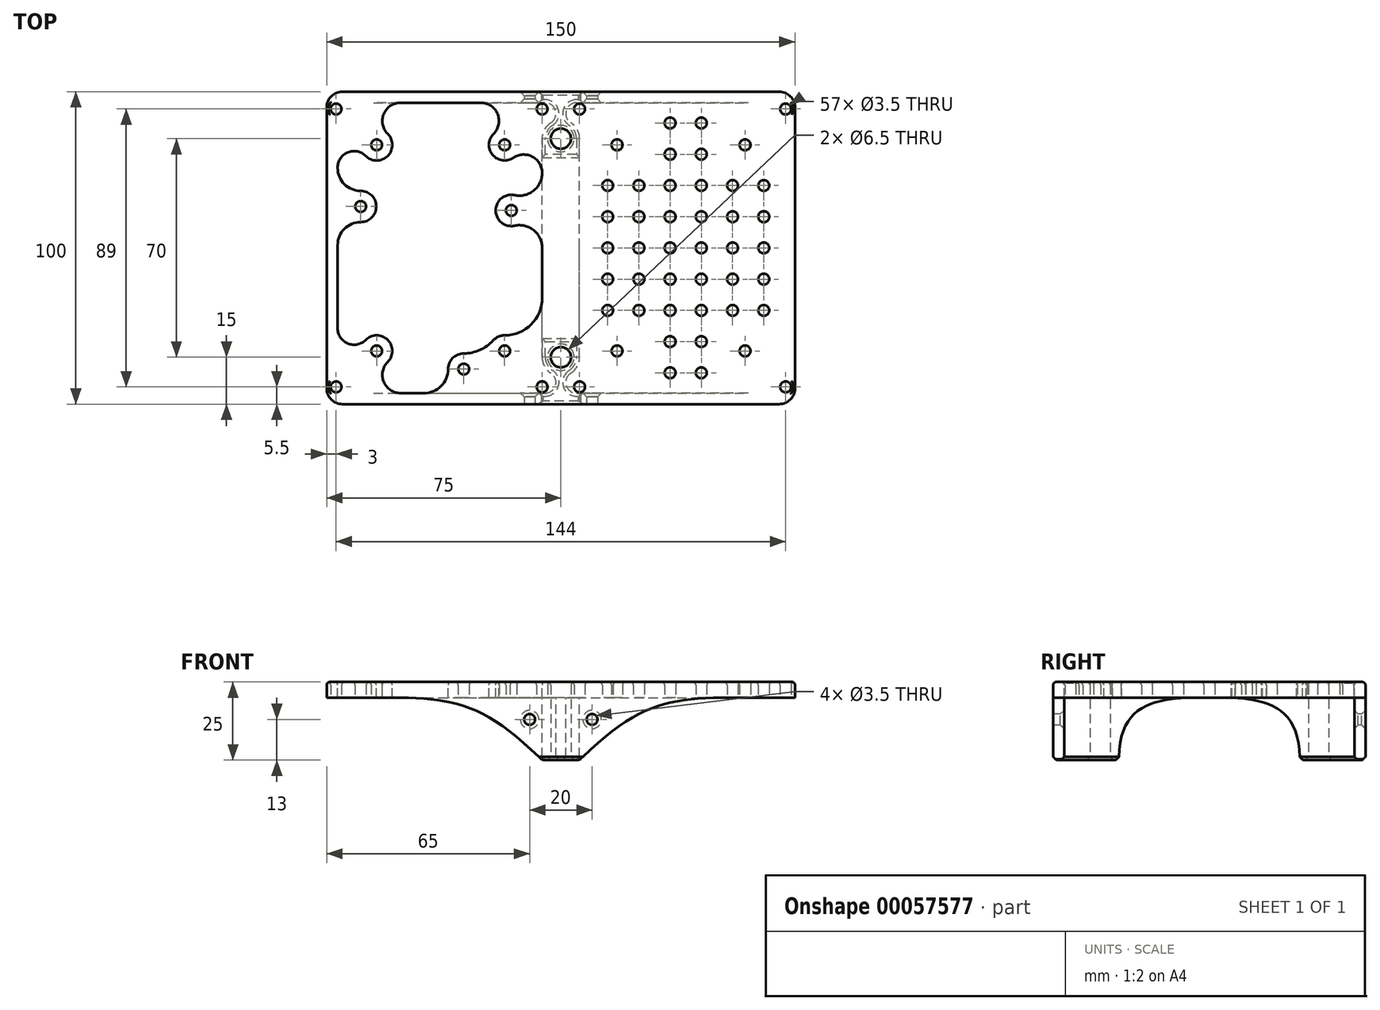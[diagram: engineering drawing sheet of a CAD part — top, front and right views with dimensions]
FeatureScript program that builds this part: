
annotation { "Feature Type Name" : "Feature", "Feature Type Description" : "" }
export const myFeature = defineFeature(function(context is Context, id is Id, definition is map)
    precondition{}
    {
        {
            var Q0;
            Q0=qCreatedBy(makeId("Top.planeOp"),FACE);
            var sketch = newSketch(context, id + "F0", { "sketchPlane" : qUnion([Q0])});
            skCircle(sketch, "E0", {"center": v(0, 35) * mm, "radius": 3.25 * mm});
            skCircle(sketch, "E1", {"center": v(0, -35) * mm, "radius": 3.25 * mm});
            skLineSegment(sketch, "E2", {"start": v(0, 35) * mm, "end": v(0, 0) * mm, "construction": true});
            skLineSegment(sketch, "E3", {"start": v(0, 0) * mm, "end": v(0, -35) * mm, "construction": true});
            skLineSegment(sketch, "E4.bottom", {"start": v(-75, 41.25) * mm, "end": v(-5, 41.25) * mm, "construction": true});
            skLineSegment(sketch, "E4.top", {"start": v(-75, -41.25) * mm, "end": v(-5, -41.25) * mm, "construction": true});
            skLineSegment(sketch, "E4.left", {"start": v(-75, 41.25) * mm, "end": v(-75, -41.25) * mm, "construction": true});
            skLineSegment(sketch, "E4.right", {"start": v(-5, 41.25) * mm, "end": v(-5, -41.25) * mm, "construction": true});
            skPoint(sketch, "E5", {"position": v(-64.13, -36.25) * mm});
            skLineSegment(sketch, "E6", {"start": v(-75, -36.25) * mm, "end": v(-5, -36.25) * mm, "construction": true});
            skCircle(sketch, "E7", {"center": v(-31.1, -38.8) * mm, "radius": 1.75 * mm});
            skCircle(sketch, "E8", {"center": v(-64.13, 13.28) * mm, "radius": 1.75 * mm});
            skCircle(sketch, "E9", {"center": v(-15.87, 12) * mm, "radius": 1.75 * mm});
            skPoint(sketch, "E10", {"position": v(-15.87, -36.25) * mm});
            skLineSegment(sketch, "E11", {"start": v(-75, 16.69) * mm, "end": v(-5, 16.7) * mm, "construction": true});
            skCircle(sketch, "E12", {"center": v(0, 0) * mm, "radius": 75 * mm, "construction": true});
            skLineSegment(sketch, "E13.rect.bottom", {"start": v(75, 50) * mm, "end": v(-75, 50) * mm});
            skLineSegment(sketch, "E13.rect.top", {"start": v(75, -50) * mm, "end": v(-75, -50) * mm});
            skLineSegment(sketch, "E13.rect.left", {"start": v(75, 50) * mm, "end": v(75, -50) * mm});
            skLineSegment(sketch, "E13.rect.right", {"start": v(-75, 50) * mm, "end": v(-75, -50) * mm});
            skCircle(sketch, "E14", {"center": v(0, -35) * mm, "radius": 6 * mm, "construction": true});
            skCircle(sketch, "E15", {"center": v(0, 35) * mm, "radius": 6 * mm, "construction": true});
            skLineSegment(sketch, "E16.bottom", {"start": v(-62, 36) * mm, "end": v(-15, 36) * mm, "construction": true});
            skLineSegment(sketch, "E16.top", {"start": v(-62, -36) * mm, "end": v(-15, -36) * mm, "construction": true});
            skLineSegment(sketch, "E16.left", {"start": v(-62, 36) * mm, "end": v(-62, -36) * mm, "construction": true});
            skLineSegment(sketch, "E16.right", {"start": v(-15, 36) * mm, "end": v(-15, -36) * mm, "construction": true});
            skLineSegment(sketch, "E17.0", {"start": v(-59, 33) * mm, "end": v(-18, 33) * mm, "construction": true});
            skLineSegment(sketch, "E17.1", {"start": v(-59, 33) * mm, "end": v(-59, -33) * mm, "construction": true});
            skLineSegment(sketch, "E17.2", {"start": v(-59, -33) * mm, "end": v(-18, -33) * mm, "construction": true});
            skLineSegment(sketch, "E17.3", {"start": v(-18, 33) * mm, "end": v(-18, -33) * mm, "construction": true});
            skCircle(sketch, "E18", {"center": v(-59, 33) * mm, "radius": 1.75 * mm});
            skCircle(sketch, "E19", {"center": v(-18, 33) * mm, "radius": 1.75 * mm});
            skCircle(sketch, "E20", {"center": v(-59, -33) * mm, "radius": 1.75 * mm});
            skCircle(sketch, "E21", {"center": v(-18, -33) * mm, "radius": 1.75 * mm});
            skLineSegment(sketch, "E22.bottom", {"start": v(-75, 47.5) * mm, "end": v(-3, 47.5) * mm, "construction": true});
            skLineSegment(sketch, "E22.top", {"start": v(-75, -47.5) * mm, "end": v(-3, -47.5) * mm, "construction": true});
            skLineSegment(sketch, "E22.left", {"start": v(-75, 47.5) * mm, "end": v(-75, -47.5) * mm, "construction": true});
            skLineSegment(sketch, "E22.right", {"start": v(-3, 47.5) * mm, "end": v(-3, -47.5) * mm, "construction": true});
            skLineSegment(sketch, "E23.0", {"start": v(-72, 44.5) * mm, "end": v(-72, -44.5) * mm, "construction": true});
            skLineSegment(sketch, "E23.1", {"start": v(-72, 44.5) * mm, "end": v(-6, 44.5) * mm, "construction": true});
            skLineSegment(sketch, "E23.2", {"start": v(-6, 44.5) * mm, "end": v(-6, -44.5) * mm, "construction": true});
            skLineSegment(sketch, "E23.3", {"start": v(-72, -44.5) * mm, "end": v(-6, -44.5) * mm, "construction": true});
            skCircle(sketch, "E24", {"center": v(-72, 44.5) * mm, "radius": 1.75 * mm});
            skCircle(sketch, "E25", {"center": v(-6, 44.5) * mm, "radius": 1.75 * mm});
            skCircle(sketch, "E26", {"center": v(-72, -44.5) * mm, "radius": 1.75 * mm});
            skCircle(sketch, "E27", {"center": v(-6, -44.5) * mm, "radius": 1.75 * mm});
            skCircle(sketch, "E28.MirrorC", {"center": v(72, 44.5) * mm, "radius": 1.75 * mm});
            skCircle(sketch, "E29.MirrorC", {"center": v(6, 44.5) * mm, "radius": 1.75 * mm});
            skCircle(sketch, "E30.MirrorC", {"center": v(59, 33) * mm, "radius": 1.75 * mm});
            skCircle(sketch, "E31.MirrorC", {"center": v(18, 33) * mm, "radius": 1.75 * mm});
            skCircle(sketch, "E32.MirrorC", {"center": v(59, -33) * mm, "radius": 1.75 * mm});
            skCircle(sketch, "E33.MirrorC", {"center": v(18, -33) * mm, "radius": 1.75 * mm});
            skCircle(sketch, "E34.MirrorC", {"center": v(6, -44.5) * mm, "radius": 1.75 * mm});
            skCircle(sketch, "E35.MirrorC", {"center": v(72, -44.5) * mm, "radius": 1.75 * mm});
            skCircle(sketch, "E36", {"center": v(65, 40) * mm, "radius": 1.75 * mm, "construction": true});
            skCircle(sketch, "E37.0.1.0", {"center": v(65, 30) * mm, "radius": 1.75 * mm, "construction": true});
            skCircle(sketch, "E37.0.2.0", {"center": v(65, 20) * mm, "radius": 1.75 * mm});
            skCircle(sketch, "E37.0.3.0", {"center": v(65, 10) * mm, "radius": 1.75 * mm});
            skCircle(sketch, "E37.0.4.0", {"center": v(65, 0) * mm, "radius": 1.75 * mm});
            skCircle(sketch, "E37.0.5.0", {"center": v(65, -10) * mm, "radius": 1.75 * mm});
            skCircle(sketch, "E37.0.6.0", {"center": v(65, -20) * mm, "radius": 1.75 * mm});
            skCircle(sketch, "E37.0.7.0", {"center": v(65, -30) * mm, "radius": 1.75 * mm, "construction": true});
            skCircle(sketch, "E37.0.8.0", {"center": v(65, -40) * mm, "radius": 1.75 * mm, "construction": true});
            skCircle(sketch, "E37.1.0.0", {"center": v(55, 40) * mm, "radius": 1.75 * mm, "construction": true});
            skCircle(sketch, "E37.1.1.0", {"center": v(55, 30) * mm, "radius": 1.75 * mm, "construction": true});
            skCircle(sketch, "E37.1.2.0", {"center": v(55, 20) * mm, "radius": 1.75 * mm});
            skCircle(sketch, "E37.1.3.0", {"center": v(55, 10) * mm, "radius": 1.75 * mm});
            skCircle(sketch, "E37.1.4.0", {"center": v(55, 0) * mm, "radius": 1.75 * mm});
            skCircle(sketch, "E37.1.5.0", {"center": v(55, -10) * mm, "radius": 1.75 * mm});
            skCircle(sketch, "E37.1.6.0", {"center": v(55, -20) * mm, "radius": 1.75 * mm});
            skCircle(sketch, "E37.1.7.0", {"center": v(55, -30) * mm, "radius": 1.75 * mm, "construction": true});
            skCircle(sketch, "E37.1.8.0", {"center": v(55, -40) * mm, "radius": 1.75 * mm, "construction": true});
            skCircle(sketch, "E37.2.0.0", {"center": v(45, 40) * mm, "radius": 1.75 * mm});
            skCircle(sketch, "E37.2.1.0", {"center": v(45, 30) * mm, "radius": 1.75 * mm});
            skCircle(sketch, "E37.2.2.0", {"center": v(45, 20) * mm, "radius": 1.75 * mm});
            skCircle(sketch, "E37.2.3.0", {"center": v(45, 10) * mm, "radius": 1.75 * mm});
            skCircle(sketch, "E37.2.4.0", {"center": v(45, 0) * mm, "radius": 1.75 * mm});
            skCircle(sketch, "E37.2.5.0", {"center": v(45, -10) * mm, "radius": 1.75 * mm});
            skCircle(sketch, "E37.2.6.0", {"center": v(45, -20) * mm, "radius": 1.75 * mm});
            skCircle(sketch, "E37.2.7.0", {"center": v(45, -30) * mm, "radius": 1.75 * mm});
            skCircle(sketch, "E37.2.8.0", {"center": v(45, -40) * mm, "radius": 1.75 * mm});
            skCircle(sketch, "E37.3.0.0", {"center": v(35, 40) * mm, "radius": 1.75 * mm});
            skCircle(sketch, "E37.3.1.0", {"center": v(35, 30) * mm, "radius": 1.75 * mm});
            skCircle(sketch, "E37.3.2.0", {"center": v(35, 20) * mm, "radius": 1.75 * mm});
            skCircle(sketch, "E37.3.3.0", {"center": v(35, 10) * mm, "radius": 1.75 * mm});
            skCircle(sketch, "E37.3.4.0", {"center": v(35, 0) * mm, "radius": 1.75 * mm});
            skCircle(sketch, "E37.3.5.0", {"center": v(35, -10) * mm, "radius": 1.75 * mm});
            skCircle(sketch, "E37.3.6.0", {"center": v(35, -20) * mm, "radius": 1.75 * mm});
            skCircle(sketch, "E37.3.7.0", {"center": v(35, -30) * mm, "radius": 1.75 * mm});
            skCircle(sketch, "E37.3.8.0", {"center": v(35, -40) * mm, "radius": 1.75 * mm});
            skCircle(sketch, "E37.4.0.0", {"center": v(25, 40) * mm, "radius": 1.75 * mm, "construction": true});
            skCircle(sketch, "E37.4.1.0", {"center": v(25, 30) * mm, "radius": 1.75 * mm, "construction": true});
            skCircle(sketch, "E37.4.2.0", {"center": v(25, 20) * mm, "radius": 1.75 * mm});
            skCircle(sketch, "E37.4.3.0", {"center": v(25, 10) * mm, "radius": 1.75 * mm});
            skCircle(sketch, "E37.4.4.0", {"center": v(25, 0) * mm, "radius": 1.75 * mm});
            skCircle(sketch, "E37.4.5.0", {"center": v(25, -10) * mm, "radius": 1.75 * mm});
            skCircle(sketch, "E37.4.6.0", {"center": v(25, -20) * mm, "radius": 1.75 * mm});
            skCircle(sketch, "E37.4.7.0", {"center": v(25, -30) * mm, "radius": 1.75 * mm, "construction": true});
            skCircle(sketch, "E37.4.8.0", {"center": v(25, -40) * mm, "radius": 1.75 * mm, "construction": true});
            skCircle(sketch, "E37.5.0.0", {"center": v(15, 40) * mm, "radius": 1.75 * mm, "construction": true});
            skCircle(sketch, "E37.5.1.0", {"center": v(15, 30) * mm, "radius": 1.75 * mm, "construction": true});
            skCircle(sketch, "E37.5.2.0", {"center": v(15, 20) * mm, "radius": 1.75 * mm});
            skCircle(sketch, "E37.5.3.0", {"center": v(15, 10) * mm, "radius": 1.75 * mm});
            skCircle(sketch, "E37.5.4.0", {"center": v(15, 0) * mm, "radius": 1.75 * mm});
            skCircle(sketch, "E37.5.5.0", {"center": v(15, -10) * mm, "radius": 1.75 * mm});
            skCircle(sketch, "E37.5.6.0", {"center": v(15, -20) * mm, "radius": 1.75 * mm});
            skCircle(sketch, "E37.5.7.0", {"center": v(15, -30) * mm, "radius": 1.75 * mm, "construction": true});
            skCircle(sketch, "E37.5.8.0", {"center": v(15, -40) * mm, "radius": 1.75 * mm, "construction": true});
            skCircle(sketch, "E37.6.0.0", {"center": v(5, 40) * mm, "radius": 1.75 * mm, "construction": true});
            skCircle(sketch, "E37.6.1.0", {"center": v(5, 30) * mm, "radius": 1.75 * mm, "construction": true});
            skCircle(sketch, "E37.6.2.0", {"center": v(5, 20) * mm, "radius": 1.75 * mm, "construction": true});
            skCircle(sketch, "E37.6.3.0", {"center": v(5, 10) * mm, "radius": 1.75 * mm, "construction": true});
            skCircle(sketch, "E37.6.4.0", {"center": v(5, 0) * mm, "radius": 1.75 * mm, "construction": true});
            skCircle(sketch, "E37.6.5.0", {"center": v(5, -10) * mm, "radius": 1.75 * mm, "construction": true});
            skCircle(sketch, "E37.6.6.0", {"center": v(5, -20) * mm, "radius": 1.75 * mm, "construction": true});
            skCircle(sketch, "E37.6.7.0", {"center": v(5, -30) * mm, "radius": 1.75 * mm, "construction": true});
            skCircle(sketch, "E37.6.8.0", {"center": v(5, -40) * mm, "radius": 1.75 * mm, "construction": true});
            skLineSegment(sketch, "E37.direction1", {"start": v(65, 40) * mm, "end": v(55, 40) * mm, "construction": true});
            skLineSegment(sketch, "E37.direction2", {"start": v(65, 40) * mm, "end": v(65, 30) * mm, "construction": true});
            skSolve(sketch);
        }
        {
            var Q0;
            Q0 = qSketchRegion(id + "F0", true);
            extrude(context, id + "F1", {"entities" : qUnion([Q0]), "depth" : 5 * mm});
        }
        {
            var Q0;
            Q0=makeQuery(id+"F1.opExtrude","SWEPT_EDGE",EDGE,{"disambiguationData":[OSD([sQuery(id+"F0.wireOp",EDGE,"E13.rect.bottom"),sQuery(id+"F0.wireOp",EDGE,"E13.rect.right")])]});
            var Q1;
            Q1=makeQuery(id+"F1.opExtrude","SWEPT_EDGE",EDGE,{"disambiguationData":[OSD([sQuery(id+"F0.wireOp",EDGE,"E13.rect.top"),sQuery(id+"F0.wireOp",EDGE,"E13.rect.right")])]});
            var Q2;
            Q2=makeQuery(id+"F1.opExtrude","SWEPT_EDGE",EDGE,{"disambiguationData":[OSD([sQuery(id+"F0.wireOp",EDGE,"E13.rect.bottom"),sQuery(id+"F0.wireOp",EDGE,"E13.rect.left")])]});
            var Q3;
            Q3=makeQuery(id+"F1.opExtrude","SWEPT_EDGE",EDGE,{"disambiguationData":[OSD([sQuery(id+"F0.wireOp",EDGE,"E13.rect.top"),sQuery(id+"F0.wireOp",EDGE,"E13.rect.left")])]});
            fillet(context, id + "F2", {"entities" : qUnion([Q0, Q1, Q2, Q3]), "radius" : 5 * mm, "tangentPropagation" : true, "allowEdgeOverflow" : false});
        }
        {
            var Q0;
            Q0=makeQuery(id+"F1.opExtrude","CAP_FACE",FACE,{"disambiguationData":[OSD([sQuery(id+"F0.wireOp",EDGE,"E0"),sQuery(id+"F0.wireOp",EDGE,"E1"),sQuery(id+"F0.wireOp",EDGE,"E7"),sQuery(id+"F0.wireOp",EDGE,"E8"),sQuery(id+"F0.wireOp",EDGE,"E9"),sQuery(id+"F0.wireOp",EDGE,"E13.rect.bottom"),sQuery(id+"F0.wireOp",EDGE,"E13.rect.top"),sQuery(id+"F0.wireOp",EDGE,"E13.rect.left"),sQuery(id+"F0.wireOp",EDGE,"E13.rect.right"),sQuery(id+"F0.wireOp",EDGE,"E18"),sQuery(id+"F0.wireOp",EDGE,"E19"),sQuery(id+"F0.wireOp",EDGE,"E20"),sQuery(id+"F0.wireOp",EDGE,"E21"),sQuery(id+"F0.wireOp",EDGE,"E24"),sQuery(id+"F0.wireOp",EDGE,"E25"),sQuery(id+"F0.wireOp",EDGE,"E26"),sQuery(id+"F0.wireOp",EDGE,"E27"),sQuery(id+"F0.wireOp",EDGE,"E28.MirrorC"),sQuery(id+"F0.wireOp",EDGE,"E29.MirrorC"),sQuery(id+"F0.wireOp",EDGE,"E30.MirrorC"),sQuery(id+"F0.wireOp",EDGE,"E31.MirrorC"),sQuery(id+"F0.wireOp",EDGE,"E32.MirrorC"),sQuery(id+"F0.wireOp",EDGE,"E33.MirrorC"),sQuery(id+"F0.wireOp",EDGE,"E34.MirrorC"),sQuery(id+"F0.wireOp",EDGE,"E35.MirrorC"),sQuery(id+"F0.wireOp",EDGE,"E37.0.2.0"),sQuery(id+"F0.wireOp",EDGE,"E37.0.3.0"),sQuery(id+"F0.wireOp",EDGE,"E37.0.4.0"),sQuery(id+"F0.wireOp",EDGE,"E37.0.5.0"),sQuery(id+"F0.wireOp",EDGE,"E37.0.6.0"),sQuery(id+"F0.wireOp",EDGE,"E37.1.2.0"),sQuery(id+"F0.wireOp",EDGE,"E37.1.3.0"),sQuery(id+"F0.wireOp",EDGE,"E37.1.4.0"),sQuery(id+"F0.wireOp",EDGE,"E37.1.5.0"),sQuery(id+"F0.wireOp",EDGE,"E37.1.6.0"),sQuery(id+"F0.wireOp",EDGE,"E37.2.0.0"),sQuery(id+"F0.wireOp",EDGE,"E37.2.1.0"),sQuery(id+"F0.wireOp",EDGE,"E37.2.2.0"),sQuery(id+"F0.wireOp",EDGE,"E37.2.3.0"),sQuery(id+"F0.wireOp",EDGE,"E37.2.4.0"),sQuery(id+"F0.wireOp",EDGE,"E37.2.5.0"),sQuery(id+"F0.wireOp",EDGE,"E37.2.6.0"),sQuery(id+"F0.wireOp",EDGE,"E37.2.7.0"),sQuery(id+"F0.wireOp",EDGE,"E37.2.8.0"),sQuery(id+"F0.wireOp",EDGE,"E37.3.0.0"),sQuery(id+"F0.wireOp",EDGE,"E37.3.1.0"),sQuery(id+"F0.wireOp",EDGE,"E37.3.2.0"),sQuery(id+"F0.wireOp",EDGE,"E37.3.3.0"),sQuery(id+"F0.wireOp",EDGE,"E37.3.4.0"),sQuery(id+"F0.wireOp",EDGE,"E37.3.5.0"),sQuery(id+"F0.wireOp",EDGE,"E37.3.6.0"),sQuery(id+"F0.wireOp",EDGE,"E37.3.7.0"),sQuery(id+"F0.wireOp",EDGE,"E37.3.8.0"),sQuery(id+"F0.wireOp",EDGE,"E37.4.2.0"),sQuery(id+"F0.wireOp",EDGE,"E37.4.3.0"),sQuery(id+"F0.wireOp",EDGE,"E37.4.4.0"),sQuery(id+"F0.wireOp",EDGE,"E37.4.5.0"),sQuery(id+"F0.wireOp",EDGE,"E37.4.6.0"),sQuery(id+"F0.wireOp",EDGE,"E37.5.2.0"),sQuery(id+"F0.wireOp",EDGE,"E37.5.3.0"),sQuery(id+"F0.wireOp",EDGE,"E37.5.4.0"),sQuery(id+"F0.wireOp",EDGE,"E37.5.5.0"),sQuery(id+"F0.wireOp",EDGE,"E37.5.6.0")])],"isStart":false});
            var sketch = newSketch(context, id + "F3", { "sketchPlane" : qUnion([Q0])});
            skCircle(sketch, "E38", {"center": v(-59, 33) * mm, "radius": 5 * mm, "construction": true});
            skCircle(sketch, "E39", {"center": v(-64.13, 13.28) * mm, "radius": 5 * mm, "construction": true});
            skCircle(sketch, "E40", {"center": v(-18, 33) * mm, "radius": 5 * mm, "construction": true});
            skCircle(sketch, "E41", {"center": v(-15.87, 12) * mm, "radius": 5 * mm, "construction": true});
            skCircle(sketch, "E42", {"center": v(-18, -33) * mm, "radius": 5 * mm, "construction": true});
            skCircle(sketch, "E43", {"center": v(-31.1, -38.8) * mm, "radius": 5 * mm, "construction": true});
            skCircle(sketch, "E44", {"center": v(-59, -33) * mm, "radius": 5 * mm, "construction": true});
            skLineSegment(sketch, "E45.0", {"start": v(70, -46.5) * mm, "end": v(-71.5, -46.5) * mm, "construction": true});
            skLineSegment(sketch, "E45.1", {"start": v(-71.5, 46.5) * mm, "end": v(-71.5, -46.5) * mm, "construction": true});
            skLineSegment(sketch, "E45.2", {"start": v(70, 46.5) * mm, "end": v(-71.5, 46.5) * mm, "construction": true});
            skArc(sketch, "E46", {"start": v(-64.13, 8.28) * mm, "mid": v(-69.34, 6.12) * mm, "end": v(-71.5, 0.9) * mm});
            skArc(sketch, "E47", {"start": v(-71.5, -25.75) * mm, "mid": v(-68.26, -30.6) * mm, "end": v(-62.54, -29.46) * mm});
            skArc(sketch, "E48", {"start": v(-31.1, -33.8) * mm, "mid": v(-25.96, -32.7) * mm, "end": v(-21.7, -29.63) * mm});
            skLineSegment(sketch, "E49", {"start": v(-6, 46.5) * mm, "end": v(-6, -46.5) * mm, "construction": true});
            skArc(sketch, "E50", {"start": v(-18, -28) * mm, "mid": v(-9.51, -24.49) * mm, "end": v(-6, -16) * mm});
            skArc(sketch, "E51", {"start": v(-6, 0) * mm, "mid": v(-8.7, 5.67) * mm, "end": v(-14.82, 7.12) * mm});
            skArc(sketch, "E52", {"start": v(-14.82, 16.9) * mm, "mid": v(-8.7, 18.35) * mm, "end": v(-6, 24.02) * mm});
            skArc(sketch, "E53", {"start": v(-21.54, 36.54) * mm, "mid": v(-20.27, 42.9) * mm, "end": v(-25.66, 46.5) * mm});
            skArc(sketch, "E54", {"start": v(-6, 24.02) * mm, "mid": v(-9.13, 29.21) * mm, "end": v(-15.18, 28.87) * mm});
            skArc(sketch, "E55", {"start": v(-71.5, 25.65) * mm, "mid": v(-69.34, 20.44) * mm, "end": v(-64.13, 18.28) * mm});
            skArc(sketch, "E56", {"start": v(-62.54, 29.46) * mm, "mid": v(-68.26, 30.6) * mm, "end": v(-71.5, 25.75) * mm});
            skArc(sketch, "E57", {"start": v(-51.34, 46.5) * mm, "mid": v(-56.73, 42.9) * mm, "end": v(-55.46, 36.54) * mm});
            skArc(sketch, "E58", {"start": v(-55.46, -36.54) * mm, "mid": v(-56.73, -42.9) * mm, "end": v(-51.34, -46.5) * mm});
            skArc(sketch, "E59", {"start": v(-43.82, -46.5) * mm, "mid": v(-38.37, -44.24) * mm, "end": v(-36.1, -38.8) * mm});
            skLineSegment(sketch, "E60", {"start": v(-66.25, -25.75) * mm, "end": v(-59, -33) * mm, "construction": true});
            skLineSegment(sketch, "E61", {"start": v(-59, -33) * mm, "end": v(-51.34, -40.66) * mm, "construction": true});
            skArc(sketch, "E62", {"start": v(-55.46, -36.54) * mm, "mid": v(-55.46, -29.46) * mm, "end": v(-62.54, -29.46) * mm});
            skLineSegment(sketch, "E63", {"start": v(-71.5, 25.65) * mm, "end": v(-71.5, 25.75) * mm});
            skLineSegment(sketch, "E64", {"start": v(-64.13, 18.28) * mm, "end": v(-64.13, 18.28) * mm});
            skArc(sketch, "E65", {"start": v(-64.13, 8.28) * mm, "mid": v(-59.13, 13.28) * mm, "end": v(-64.13, 18.28) * mm});
            skLineSegment(sketch, "E66", {"start": v(-71.5, 0.9) * mm, "end": v(-71.5, -25.75) * mm});
            skLineSegment(sketch, "E67", {"start": v(-51.34, -46.5) * mm, "end": v(-43.82, -46.5) * mm, "construction": true});
            skLineSegment(sketch, "E68", {"start": v(-51.34, 46.5) * mm, "end": v(-25.66, 46.5) * mm});
            skArc(sketch, "E69", {"start": v(-55.46, 36.54) * mm, "mid": v(-55.46, 29.46) * mm, "end": v(-62.54, 29.46) * mm});
            skArc(sketch, "E70", {"start": v(-15.18, 28.87) * mm, "mid": v(-21.85, 29.8) * mm, "end": v(-21.54, 36.54) * mm});
            skArc(sketch, "E71", {"start": v(-14.82, 7.12) * mm, "mid": v(-20.87, 12) * mm, "end": v(-14.82, 16.9) * mm});
            skArc(sketch, "E72", {"start": v(-36.1, -38.8) * mm, "mid": v(-34.65, -35.25) * mm, "end": v(-31.1, -33.8) * mm});
            skArc(sketch, "E73", {"start": v(-21.7, -29.63) * mm, "mid": v(-20.02, -28.43) * mm, "end": v(-18, -28) * mm});
            skLineSegment(sketch, "E74", {"start": v(-6, -16) * mm, "end": v(-6, 0) * mm});
            skLineSegment(sketch, "E75", {"start": v(-51.34, -46.5) * mm, "end": v(-43.82, -46.5) * mm});
            skSolve(sketch);
        }
        {
            var Q0;
            Q0 = qSketchRegion(id + "F3", true);
            extrude(context, id + "F4", {"entities" : qUnion([Q0]), "operationType" : NewBodyOperationType.REMOVE, "endBound" : BoundingType.THROUGH_ALL, "oppositeDirection" : true, "depth" : 25 * mm});
        }
        {
            var Q0;
            Q0=makeQuery(id+"F1.opExtrude","CAP_FACE",FACE,{"disambiguationData":[OSD([sQuery(id+"F0.wireOp",EDGE,"E0"),sQuery(id+"F0.wireOp",EDGE,"E1"),sQuery(id+"F0.wireOp",EDGE,"E7"),sQuery(id+"F0.wireOp",EDGE,"E8"),sQuery(id+"F0.wireOp",EDGE,"E9"),sQuery(id+"F0.wireOp",EDGE,"E13.rect.bottom"),sQuery(id+"F0.wireOp",EDGE,"E13.rect.top"),sQuery(id+"F0.wireOp",EDGE,"E13.rect.left"),sQuery(id+"F0.wireOp",EDGE,"E13.rect.right"),sQuery(id+"F0.wireOp",EDGE,"E18"),sQuery(id+"F0.wireOp",EDGE,"E19"),sQuery(id+"F0.wireOp",EDGE,"E20"),sQuery(id+"F0.wireOp",EDGE,"E21"),sQuery(id+"F0.wireOp",EDGE,"E24"),sQuery(id+"F0.wireOp",EDGE,"E25"),sQuery(id+"F0.wireOp",EDGE,"E26"),sQuery(id+"F0.wireOp",EDGE,"E27"),sQuery(id+"F0.wireOp",EDGE,"E28.MirrorC"),sQuery(id+"F0.wireOp",EDGE,"E29.MirrorC"),sQuery(id+"F0.wireOp",EDGE,"E30.MirrorC"),sQuery(id+"F0.wireOp",EDGE,"E31.MirrorC"),sQuery(id+"F0.wireOp",EDGE,"E32.MirrorC"),sQuery(id+"F0.wireOp",EDGE,"E33.MirrorC"),sQuery(id+"F0.wireOp",EDGE,"E34.MirrorC"),sQuery(id+"F0.wireOp",EDGE,"E35.MirrorC"),sQuery(id+"F0.wireOp",EDGE,"E37.0.2.0"),sQuery(id+"F0.wireOp",EDGE,"E37.0.3.0"),sQuery(id+"F0.wireOp",EDGE,"E37.0.4.0"),sQuery(id+"F0.wireOp",EDGE,"E37.0.5.0"),sQuery(id+"F0.wireOp",EDGE,"E37.0.6.0"),sQuery(id+"F0.wireOp",EDGE,"E37.1.2.0"),sQuery(id+"F0.wireOp",EDGE,"E37.1.3.0"),sQuery(id+"F0.wireOp",EDGE,"E37.1.4.0"),sQuery(id+"F0.wireOp",EDGE,"E37.1.5.0"),sQuery(id+"F0.wireOp",EDGE,"E37.1.6.0"),sQuery(id+"F0.wireOp",EDGE,"E37.2.0.0"),sQuery(id+"F0.wireOp",EDGE,"E37.2.1.0"),sQuery(id+"F0.wireOp",EDGE,"E37.2.2.0"),sQuery(id+"F0.wireOp",EDGE,"E37.2.3.0"),sQuery(id+"F0.wireOp",EDGE,"E37.2.4.0"),sQuery(id+"F0.wireOp",EDGE,"E37.2.5.0"),sQuery(id+"F0.wireOp",EDGE,"E37.2.6.0"),sQuery(id+"F0.wireOp",EDGE,"E37.2.7.0"),sQuery(id+"F0.wireOp",EDGE,"E37.2.8.0"),sQuery(id+"F0.wireOp",EDGE,"E37.3.0.0"),sQuery(id+"F0.wireOp",EDGE,"E37.3.1.0"),sQuery(id+"F0.wireOp",EDGE,"E37.3.2.0"),sQuery(id+"F0.wireOp",EDGE,"E37.3.3.0"),sQuery(id+"F0.wireOp",EDGE,"E37.3.4.0"),sQuery(id+"F0.wireOp",EDGE,"E37.3.5.0"),sQuery(id+"F0.wireOp",EDGE,"E37.3.6.0"),sQuery(id+"F0.wireOp",EDGE,"E37.3.7.0"),sQuery(id+"F0.wireOp",EDGE,"E37.3.8.0"),sQuery(id+"F0.wireOp",EDGE,"E37.4.2.0"),sQuery(id+"F0.wireOp",EDGE,"E37.4.3.0"),sQuery(id+"F0.wireOp",EDGE,"E37.4.4.0"),sQuery(id+"F0.wireOp",EDGE,"E37.4.5.0"),sQuery(id+"F0.wireOp",EDGE,"E37.4.6.0"),sQuery(id+"F0.wireOp",EDGE,"E37.5.2.0"),sQuery(id+"F0.wireOp",EDGE,"E37.5.3.0"),sQuery(id+"F0.wireOp",EDGE,"E37.5.4.0"),sQuery(id+"F0.wireOp",EDGE,"E37.5.5.0"),sQuery(id+"F0.wireOp",EDGE,"E37.5.6.0")])],"isStart":true});
            var sketch = newSketch(context, id + "F5", { "sketchPlane" : qUnion([Q0])});
            skArc(sketch, "E76", {"start": v(-6, 35) * mm, "mid": v(0, 41) * mm, "end": v(6, 35) * mm, "construction": true});
            skArc(sketch, "E77", {"start": v(6, -35) * mm, "mid": v(0, -41) * mm, "end": v(-6, -35) * mm, "construction": true});
            skLineSegment(sketch, "E78", {"start": v(-6, 35) * mm, "end": v(-6, -35) * mm});
            skLineSegment(sketch, "E79", {"start": v(6, 35) * mm, "end": v(6, -35) * mm});
            skLineSegment(sketch, "E80.bottom", {"start": v(-60, 50) * mm, "end": v(60, 50) * mm});
            skLineSegment(sketch, "E80.top", {"start": v(-60, 46.5) * mm, "end": v(60, 46.5) * mm, "construction": true});
            skLineSegment(sketch, "E80.left", {"start": v(-60, 50) * mm, "end": v(-60, 46.5) * mm});
            skLineSegment(sketch, "E80.right", {"start": v(60, 50) * mm, "end": v(60, 46.5) * mm});
            skLineSegment(sketch, "E81.bottom", {"start": v(-60, -50) * mm, "end": v(60, -50) * mm});
            skLineSegment(sketch, "E81.top", {"start": v(-60, -46.5) * mm, "end": v(60, -46.5) * mm, "construction": true});
            skLineSegment(sketch, "E81.left", {"start": v(-60, -50) * mm, "end": v(-60, -46.5) * mm});
            skLineSegment(sketch, "E81.right", {"start": v(60, -50) * mm, "end": v(60, -46.5) * mm});
            skPoint(sketch, "E82", {"position": v(0, 46.5) * mm});
            skPoint(sketch, "E83", {"position": v(0, -46.5) * mm});
            skArc(sketch, "E84", {"start": v(-3.2, 40.07) * mm, "mid": v(-1.72, 43.99) * mm, "end": v(-5.06, 46.5) * mm});
            skPoint(sketch, "E85", {"position": v(-6, 44.5) * mm});
            skLineSegment(sketch, "E86", {"start": v(-6, 44.5) * mm, "end": v(-5.06, 43.02) * mm, "construction": true});
            skLineSegment(sketch, "E87", {"start": v(-3.2, 40.07) * mm, "end": v(-5.06, 43.02) * mm, "construction": true});
            skArc(sketch, "E88.MirrorCS", {"start": v(3.2, 40.07) * mm, "mid": v(1.72, 43.99) * mm, "end": v(5.06, 46.5) * mm});
            skArc(sketch, "E89.MirrorCS", {"start": v(-3.2, -40.07) * mm, "mid": v(-1.72, -43.99) * mm, "end": v(-5.06, -46.5) * mm});
            skArc(sketch, "E90.MirrorCS", {"start": v(3.2, -40.07) * mm, "mid": v(1.72, -43.99) * mm, "end": v(5.06, -46.5) * mm});
            skLineSegment(sketch, "E91", {"start": v(-5.06, -46.5) * mm, "end": v(-60, -46.5) * mm});
            skLineSegment(sketch, "E92", {"start": v(5.06, -46.5) * mm, "end": v(60, -46.5) * mm});
            skLineSegment(sketch, "E93", {"start": v(-60, 46.5) * mm, "end": v(-5.06, 46.5) * mm});
            skLineSegment(sketch, "E94", {"start": v(5.06, 46.5) * mm, "end": v(60, 46.5) * mm});
            skArc(sketch, "E95", {"start": v(-6, 35) * mm, "mid": v(-5.25, 37.9) * mm, "end": v(-3.2, 40.07) * mm});
            skArc(sketch, "E96", {"start": v(3.2, 40.07) * mm, "mid": v(5.25, 37.9) * mm, "end": v(6, 35) * mm});
            skArc(sketch, "E97", {"start": v(6, -35) * mm, "mid": v(5.25, -37.9) * mm, "end": v(3.2, -40.07) * mm});
            skArc(sketch, "E98", {"start": v(-3.2, -40.07) * mm, "mid": v(-5.25, -37.9) * mm, "end": v(-6, -35) * mm});
            skCircle(sketch, "E99.0", {"center": v(0, -35) * mm, "radius": 3.25 * mm});
            skCircle(sketch, "E99.1", {"center": v(0, 35) * mm, "radius": 3.25 * mm});
            skSolve(sketch);
        }
        {
            var Q0;
            Q0 = qSketchRegion(id + "F5", true);
            extrude(context, id + "F6", {"entities" : qUnion([Q0]), "operationType" : NewBodyOperationType.ADD, "depth" : 20 * mm});
        }
        {
            var Q0;
            Q0=qCreatedBy(makeId("Front.planeOp"),FACE);
            var sketch = newSketch(context, id + "F7", { "sketchPlane" : qUnion([Q0])});
            skLineSegment(sketch, "E100", {"start": v(-60, 0) * mm, "end": v(-60, -20) * mm});
            skLineSegment(sketch, "E101", {"start": v(-60, -20) * mm, "end": v(-6, -20) * mm});
            skFitSpline(sketch, "E102", {"points": [v(-60, 0) * mm, v(-6, -20) * mm], "startDerivative": vector(71.9, 0) * mm, "endDerivative": vector(61.29, -60) * mm});
            skFitSpline(sketch, "E103.MirrorCS", {"points": [v(60, 0) * mm, v(6, -20) * mm], "startDerivative": vector(-71.9, 0) * mm, "endDerivative": vector(-61.29, -60) * mm});
            skLineSegment(sketch, "E104.MirrorCS", {"start": v(60, 0) * mm, "end": v(60, -20) * mm});
            skLineSegment(sketch, "E105.MirrorCS", {"start": v(60, -20) * mm, "end": v(6, -20) * mm});
            skSolve(sketch);
        }
        {
            var Q0;
            Q0 = qSketchRegion(id + "F7", true);
            extrude(context, id + "F8", {"entities" : qUnion([Q0]), "operationType" : NewBodyOperationType.REMOVE, "endBound" : BoundingType.THROUGH_ALL, "oppositeDirection" : true, "depth" : 25 * mm, "hasSecondDirection" : true, "secondDirectionBound" : SecondDirectionBoundingType.THROUGH_ALL, "secondDirectionOppositeDirection" : false, "secondDirectionDepth" : 25 * mm});
        }
        {
            var Q0;
            Q0=makeQuery(id+"F6.opExtrude","SWEPT_FACE",FACE,{"disambiguationData":[OSD([sQuery(id+"F5.wireOp",EDGE,"E79")])]});
            var sketch = newSketch(context, id + "F9", { "sketchPlane" : qUnion([Q0])});
            skFitSpline(sketch, "E106", {"points": [v(-29, -20) * mm, v(0, 0) * mm, v(29, -20) * mm], "startDerivative": vector(0, 120) * mm, "endDerivative": vector(0, -120) * mm});
            skLineSegment(sketch, "E107", {"start": v(-29, -20) * mm, "end": v(29, -20) * mm});
            skSolve(sketch);
        }
        {
            var Q0;
            Q0 = qSketchRegion(id + "F9", true);
            extrude(context, id + "F10", {"entities" : qUnion([Q0]), "operationType" : NewBodyOperationType.REMOVE, "endBound" : BoundingType.THROUGH_ALL, "oppositeDirection" : true, "depth" : 25 * mm});
        }
        {
            var Q0;
            Q0=makeQuery(id+"F1.opExtrude","CAP_FACE",FACE,{"disambiguationData":[OSD([sQuery(id+"F0.wireOp",EDGE,"E0"),sQuery(id+"F0.wireOp",EDGE,"E1"),sQuery(id+"F0.wireOp",EDGE,"E7"),sQuery(id+"F0.wireOp",EDGE,"E8"),sQuery(id+"F0.wireOp",EDGE,"E9"),sQuery(id+"F0.wireOp",EDGE,"E13.rect.bottom"),sQuery(id+"F0.wireOp",EDGE,"E13.rect.top"),sQuery(id+"F0.wireOp",EDGE,"E13.rect.left"),sQuery(id+"F0.wireOp",EDGE,"E13.rect.right"),sQuery(id+"F0.wireOp",EDGE,"E18"),sQuery(id+"F0.wireOp",EDGE,"E19"),sQuery(id+"F0.wireOp",EDGE,"E20"),sQuery(id+"F0.wireOp",EDGE,"E21"),sQuery(id+"F0.wireOp",EDGE,"E24"),sQuery(id+"F0.wireOp",EDGE,"E25"),sQuery(id+"F0.wireOp",EDGE,"E26"),sQuery(id+"F0.wireOp",EDGE,"E27"),sQuery(id+"F0.wireOp",EDGE,"E28.MirrorC"),sQuery(id+"F0.wireOp",EDGE,"E29.MirrorC"),sQuery(id+"F0.wireOp",EDGE,"E30.MirrorC"),sQuery(id+"F0.wireOp",EDGE,"E31.MirrorC"),sQuery(id+"F0.wireOp",EDGE,"E32.MirrorC"),sQuery(id+"F0.wireOp",EDGE,"E33.MirrorC"),sQuery(id+"F0.wireOp",EDGE,"E34.MirrorC"),sQuery(id+"F0.wireOp",EDGE,"E35.MirrorC"),sQuery(id+"F0.wireOp",EDGE,"E37.0.2.0"),sQuery(id+"F0.wireOp",EDGE,"E37.0.3.0"),sQuery(id+"F0.wireOp",EDGE,"E37.0.4.0"),sQuery(id+"F0.wireOp",EDGE,"E37.0.5.0"),sQuery(id+"F0.wireOp",EDGE,"E37.0.6.0"),sQuery(id+"F0.wireOp",EDGE,"E37.1.2.0"),sQuery(id+"F0.wireOp",EDGE,"E37.1.3.0"),sQuery(id+"F0.wireOp",EDGE,"E37.1.4.0"),sQuery(id+"F0.wireOp",EDGE,"E37.1.5.0"),sQuery(id+"F0.wireOp",EDGE,"E37.1.6.0"),sQuery(id+"F0.wireOp",EDGE,"E37.2.0.0"),sQuery(id+"F0.wireOp",EDGE,"E37.2.1.0"),sQuery(id+"F0.wireOp",EDGE,"E37.2.2.0"),sQuery(id+"F0.wireOp",EDGE,"E37.2.3.0"),sQuery(id+"F0.wireOp",EDGE,"E37.2.4.0"),sQuery(id+"F0.wireOp",EDGE,"E37.2.5.0"),sQuery(id+"F0.wireOp",EDGE,"E37.2.6.0"),sQuery(id+"F0.wireOp",EDGE,"E37.2.7.0"),sQuery(id+"F0.wireOp",EDGE,"E37.2.8.0"),sQuery(id+"F0.wireOp",EDGE,"E37.3.0.0"),sQuery(id+"F0.wireOp",EDGE,"E37.3.1.0"),sQuery(id+"F0.wireOp",EDGE,"E37.3.2.0"),sQuery(id+"F0.wireOp",EDGE,"E37.3.3.0"),sQuery(id+"F0.wireOp",EDGE,"E37.3.4.0"),sQuery(id+"F0.wireOp",EDGE,"E37.3.5.0"),sQuery(id+"F0.wireOp",EDGE,"E37.3.6.0"),sQuery(id+"F0.wireOp",EDGE,"E37.3.7.0"),sQuery(id+"F0.wireOp",EDGE,"E37.3.8.0"),sQuery(id+"F0.wireOp",EDGE,"E37.4.2.0"),sQuery(id+"F0.wireOp",EDGE,"E37.4.3.0"),sQuery(id+"F0.wireOp",EDGE,"E37.4.4.0"),sQuery(id+"F0.wireOp",EDGE,"E37.4.5.0"),sQuery(id+"F0.wireOp",EDGE,"E37.4.6.0"),sQuery(id+"F0.wireOp",EDGE,"E37.5.2.0"),sQuery(id+"F0.wireOp",EDGE,"E37.5.3.0"),sQuery(id+"F0.wireOp",EDGE,"E37.5.4.0"),sQuery(id+"F0.wireOp",EDGE,"E37.5.5.0"),sQuery(id+"F0.wireOp",EDGE,"E37.5.6.0")])],"isStart":false});
            fillet(context, id + "F11", {"entities" : qUnion([Q0]), "radius" : 1 * mm, "tangentPropagation" : true, "allowEdgeOverflow" : false});
        }
        {
            var Q0;
            {var subQ0=sQuery(id+"F5.wireOp",EDGE,"E84");var subQ1=sQuery(id+"F5.wireOp",EDGE,"E80.bottom");var subQ2=sQuery(id+"F5.wireOp",EDGE,"E79");var subQ3=sQuery(id+"F5.wireOp",EDGE,"E88.MirrorCS");var subQ4=sQuery(id+"F5.wireOp",EDGE,"E78");var subQ5=sQuery(id+"F5.wireOp",EDGE,"E93");var subQ6=sQuery(id+"F5.wireOp",EDGE,"E94");var subQ7=sQuery(id+"F5.wireOp",EDGE,"E95");var subQ8=sQuery(id+"F5.wireOp",EDGE,"E96");var subQ9=sQuery(id+"F5.wireOp",EDGE,"E99.1");Q0=makeQuery(id+"F10.boolean.opBoolean","SPLIT",FACE,{"disambiguationData":[TD([makeQuery(id+"F1.opExtrude","SWEPT_FACE",FACE,{"disambiguationData":[OSD([sQuery(id+"F0.wireOp",EDGE,"E1")])]})])],"derivedFrom":makeQuery(id+"F6.opExtrude","CAP_FACE",FACE,{"disambiguationData":[OSD([subQ4,subQ2,subQ1,sQuery(id+"F5.wireOp",EDGE,"E80.left"),sQuery(id+"F5.wireOp",EDGE,"E80.right"),sQuery(id+"F5.wireOp",EDGE,"E81.bottom"),sQuery(id+"F5.wireOp",EDGE,"E81.left"),sQuery(id+"F5.wireOp",EDGE,"E81.right"),subQ0,subQ3,sQuery(id+"F5.wireOp",EDGE,"E89.MirrorCS"),sQuery(id+"F5.wireOp",EDGE,"E90.MirrorCS"),sQuery(id+"F5.wireOp",EDGE,"E91"),sQuery(id+"F5.wireOp",EDGE,"E92"),subQ5,subQ6,subQ7,subQ8,sQuery(id+"F5.wireOp",EDGE,"E97"),sQuery(id+"F5.wireOp",EDGE,"E98"),sQuery(id+"F5.wireOp",EDGE,"E99.0"),subQ9])],"isStart":false})});}
            var Q1;
            {var subQ0=sQuery(id+"F5.wireOp",EDGE,"E91");var subQ1=sQuery(id+"F5.wireOp",EDGE,"E78");var subQ2=sQuery(id+"F5.wireOp",EDGE,"E90.MirrorCS");var subQ3=sQuery(id+"F5.wireOp",EDGE,"E89.MirrorCS");var subQ4=sQuery(id+"F5.wireOp",EDGE,"E81.bottom");var subQ5=sQuery(id+"F5.wireOp",EDGE,"E79");var subQ6=sQuery(id+"F5.wireOp",EDGE,"E97");var subQ7=sQuery(id+"F5.wireOp",EDGE,"E92");var subQ8=sQuery(id+"F5.wireOp",EDGE,"E98");var subQ9=sQuery(id+"F5.wireOp",EDGE,"E99.0");Q1=makeQuery(id+"F10.boolean.opBoolean","SPLIT",FACE,{"disambiguationData":[TD([makeQuery(id+"F1.opExtrude","SWEPT_FACE",FACE,{"disambiguationData":[OSD([sQuery(id+"F0.wireOp",EDGE,"E0")])]})])],"derivedFrom":makeQuery(id+"F6.opExtrude","CAP_FACE",FACE,{"disambiguationData":[OSD([subQ1,subQ5,sQuery(id+"F5.wireOp",EDGE,"E80.bottom"),sQuery(id+"F5.wireOp",EDGE,"E80.left"),sQuery(id+"F5.wireOp",EDGE,"E80.right"),subQ4,sQuery(id+"F5.wireOp",EDGE,"E81.left"),sQuery(id+"F5.wireOp",EDGE,"E81.right"),sQuery(id+"F5.wireOp",EDGE,"E84"),sQuery(id+"F5.wireOp",EDGE,"E88.MirrorCS"),subQ3,subQ2,subQ0,subQ7,sQuery(id+"F5.wireOp",EDGE,"E93"),sQuery(id+"F5.wireOp",EDGE,"E94"),sQuery(id+"F5.wireOp",EDGE,"E95"),sQuery(id+"F5.wireOp",EDGE,"E96"),subQ6,subQ8,subQ9,sQuery(id+"F5.wireOp",EDGE,"E99.1")])],"isStart":false})});}
            var Q2;
            Q2=makeQuery(id+"F1.opExtrude","CAP_FACE",FACE,{"disambiguationData":[OSD([sQuery(id+"F0.wireOp",EDGE,"E0"),sQuery(id+"F0.wireOp",EDGE,"E1"),sQuery(id+"F0.wireOp",EDGE,"E7"),sQuery(id+"F0.wireOp",EDGE,"E8"),sQuery(id+"F0.wireOp",EDGE,"E9"),sQuery(id+"F0.wireOp",EDGE,"E13.rect.bottom"),sQuery(id+"F0.wireOp",EDGE,"E13.rect.top"),sQuery(id+"F0.wireOp",EDGE,"E13.rect.left"),sQuery(id+"F0.wireOp",EDGE,"E13.rect.right"),sQuery(id+"F0.wireOp",EDGE,"E18"),sQuery(id+"F0.wireOp",EDGE,"E19"),sQuery(id+"F0.wireOp",EDGE,"E20"),sQuery(id+"F0.wireOp",EDGE,"E21"),sQuery(id+"F0.wireOp",EDGE,"E24"),sQuery(id+"F0.wireOp",EDGE,"E25"),sQuery(id+"F0.wireOp",EDGE,"E26"),sQuery(id+"F0.wireOp",EDGE,"E27"),sQuery(id+"F0.wireOp",EDGE,"E28.MirrorC"),sQuery(id+"F0.wireOp",EDGE,"E29.MirrorC"),sQuery(id+"F0.wireOp",EDGE,"E30.MirrorC"),sQuery(id+"F0.wireOp",EDGE,"E31.MirrorC"),sQuery(id+"F0.wireOp",EDGE,"E32.MirrorC"),sQuery(id+"F0.wireOp",EDGE,"E33.MirrorC"),sQuery(id+"F0.wireOp",EDGE,"E34.MirrorC"),sQuery(id+"F0.wireOp",EDGE,"E35.MirrorC"),sQuery(id+"F0.wireOp",EDGE,"E37.0.2.0"),sQuery(id+"F0.wireOp",EDGE,"E37.0.3.0"),sQuery(id+"F0.wireOp",EDGE,"E37.0.4.0"),sQuery(id+"F0.wireOp",EDGE,"E37.0.5.0"),sQuery(id+"F0.wireOp",EDGE,"E37.0.6.0"),sQuery(id+"F0.wireOp",EDGE,"E37.1.2.0"),sQuery(id+"F0.wireOp",EDGE,"E37.1.3.0"),sQuery(id+"F0.wireOp",EDGE,"E37.1.4.0"),sQuery(id+"F0.wireOp",EDGE,"E37.1.5.0"),sQuery(id+"F0.wireOp",EDGE,"E37.1.6.0"),sQuery(id+"F0.wireOp",EDGE,"E37.2.0.0"),sQuery(id+"F0.wireOp",EDGE,"E37.2.1.0"),sQuery(id+"F0.wireOp",EDGE,"E37.2.2.0"),sQuery(id+"F0.wireOp",EDGE,"E37.2.3.0"),sQuery(id+"F0.wireOp",EDGE,"E37.2.4.0"),sQuery(id+"F0.wireOp",EDGE,"E37.2.5.0"),sQuery(id+"F0.wireOp",EDGE,"E37.2.6.0"),sQuery(id+"F0.wireOp",EDGE,"E37.2.7.0"),sQuery(id+"F0.wireOp",EDGE,"E37.2.8.0"),sQuery(id+"F0.wireOp",EDGE,"E37.3.0.0"),sQuery(id+"F0.wireOp",EDGE,"E37.3.1.0"),sQuery(id+"F0.wireOp",EDGE,"E37.3.2.0"),sQuery(id+"F0.wireOp",EDGE,"E37.3.3.0"),sQuery(id+"F0.wireOp",EDGE,"E37.3.4.0"),sQuery(id+"F0.wireOp",EDGE,"E37.3.5.0"),sQuery(id+"F0.wireOp",EDGE,"E37.3.6.0"),sQuery(id+"F0.wireOp",EDGE,"E37.3.7.0"),sQuery(id+"F0.wireOp",EDGE,"E37.3.8.0"),sQuery(id+"F0.wireOp",EDGE,"E37.4.2.0"),sQuery(id+"F0.wireOp",EDGE,"E37.4.3.0"),sQuery(id+"F0.wireOp",EDGE,"E37.4.4.0"),sQuery(id+"F0.wireOp",EDGE,"E37.4.5.0"),sQuery(id+"F0.wireOp",EDGE,"E37.4.6.0"),sQuery(id+"F0.wireOp",EDGE,"E37.5.2.0"),sQuery(id+"F0.wireOp",EDGE,"E37.5.3.0"),sQuery(id+"F0.wireOp",EDGE,"E37.5.4.0"),sQuery(id+"F0.wireOp",EDGE,"E37.5.5.0"),sQuery(id+"F0.wireOp",EDGE,"E37.5.6.0")])],"isStart":false});
            chamfer(context, id + "F12", {"entities" : qUnion([Q0, Q1, Q2]), "width" : 1 * mm, "tangentPropagation" : true});
        }
        {
            var Q0;
            Q0=makeQuery(id+"F6.boolean.opBoolean","MERGE",FACE,{"derivedFrom":[makeQuery(id+"F1.opExtrude","SWEPT_FACE",FACE,{"disambiguationData":[OSD([sQuery(id+"F0.wireOp",EDGE,"E13.rect.top")])]}),makeQuery(id+"F6.opExtrude","SWEPT_FACE",FACE,{"disambiguationData":[OSD([sQuery(id+"F5.wireOp",EDGE,"E80.bottom")])]})]});
            var sketch = newSketch(context, id + "F13", { "sketchPlane" : qUnion([Q0])});
            skCircle(sketch, "E108", {"center": v(-10, -7) * mm, "radius": 1.75 * mm});
            skCircle(sketch, "E109", {"center": v(10, -7) * mm, "radius": 1.75 * mm});
            skLineSegment(sketch, "E110", {"start": v(-10, -7) * mm, "end": v(0, 0) * mm, "construction": true});
            skLineSegment(sketch, "E111", {"start": v(0, 0) * mm, "end": v(10, -7) * mm, "construction": true});
            skSolve(sketch);
        }
        {
            var Q0;
            Q0 = qSketchRegion(id + "F13", true);
            extrude(context, id + "F14", {"entities" : qUnion([Q0]), "operationType" : NewBodyOperationType.REMOVE, "endBound" : BoundingType.THROUGH_ALL, "oppositeDirection" : true, "depth" : 25 * mm});
        }
        {
            var Q0;
            Q0=makeQuery(id+"F14.boolean.opBoolean","COPY",EDGE,{"derivedFrom":makeQuery(id+"F14.opExtrude","CAP_EDGE",EDGE,{"disambiguationData":[OSD([sQuery(id+"F13.wireOp",EDGE,"E108")])],"isStart":true})});
            var Q1;
            Q1=makeQuery(id+"F14.boolean.opBoolean","COPY",EDGE,{"derivedFrom":makeQuery(id+"F14.opExtrude","CAP_EDGE",EDGE,{"disambiguationData":[OSD([sQuery(id+"F13.wireOp",EDGE,"E109")])],"isStart":true})});
            var Q2;
            Q2=makeQuery(id+"F14.boolean.opBoolean","INTERSECT",EDGE,{"derivedFrom":[makeQuery(id+"F6.opExtrude","SWEPT_FACE",FACE,{"disambiguationData":[OSD([sQuery(id+"F5.wireOp",EDGE,"E92")])]}),makeQuery(id+"F14.opExtrude","SWEPT_FACE",FACE,{"disambiguationData":[OSD([sQuery(id+"F13.wireOp",EDGE,"E109")])]})]});
            var Q3;
            Q3=makeQuery(id+"F14.boolean.opBoolean","INTERSECT",EDGE,{"derivedFrom":[makeQuery(id+"F6.boolean.opBoolean","MERGE",FACE,{"derivedFrom":[makeQuery(id+"F4.boolean.opBoolean","COPY",FACE,{"derivedFrom":makeQuery(id+"F4.opExtrude","SWEPT_FACE",FACE,{"disambiguationData":[OSD([sQuery(id+"F3.wireOp",EDGE,"E68")])]})}),makeQuery(id+"F6.opExtrude","SWEPT_FACE",FACE,{"disambiguationData":[OSD([sQuery(id+"F5.wireOp",EDGE,"E91")])]})]}),makeQuery(id+"F14.opExtrude","SWEPT_FACE",FACE,{"disambiguationData":[OSD([sQuery(id+"F13.wireOp",EDGE,"E108")])]})]});
            var Q4;
            Q4=makeQuery(id+"F14.boolean.opBoolean","INTERSECT",EDGE,{"derivedFrom":[makeQuery(id+"F6.opExtrude","SWEPT_FACE",FACE,{"disambiguationData":[OSD([sQuery(id+"F5.wireOp",EDGE,"E94")])]}),makeQuery(id+"F14.opExtrude","SWEPT_FACE",FACE,{"disambiguationData":[OSD([sQuery(id+"F13.wireOp",EDGE,"E109")])]})]});
            var Q5;
            Q5=makeQuery(id+"F14.boolean.opBoolean","INTERSECT",EDGE,{"derivedFrom":[makeQuery(id+"F6.boolean.opBoolean","MERGE",FACE,{"derivedFrom":[makeQuery(id+"F4.boolean.opBoolean","COPY",FACE,{"derivedFrom":makeQuery(id+"F4.opExtrude","SWEPT_FACE",FACE,{"disambiguationData":[OSD([sQuery(id+"F3.wireOp",EDGE,"E75")])]})}),makeQuery(id+"F6.opExtrude","SWEPT_FACE",FACE,{"disambiguationData":[OSD([sQuery(id+"F5.wireOp",EDGE,"E93")])]})]}),makeQuery(id+"F14.opExtrude","SWEPT_FACE",FACE,{"disambiguationData":[OSD([sQuery(id+"F13.wireOp",EDGE,"E108")])]})]});
            var Q6;
            Q6=makeQuery(id+"F14.boolean.opBoolean","INTERSECT",EDGE,{"derivedFrom":[makeQuery(id+"F6.boolean.opBoolean","MERGE",FACE,{"derivedFrom":[makeQuery(id+"F1.opExtrude","SWEPT_FACE",FACE,{"disambiguationData":[OSD([sQuery(id+"F0.wireOp",EDGE,"E13.rect.bottom")])]}),makeQuery(id+"F6.opExtrude","SWEPT_FACE",FACE,{"disambiguationData":[OSD([sQuery(id+"F5.wireOp",EDGE,"E81.bottom")])]})]}),makeQuery(id+"F14.opExtrude","SWEPT_FACE",FACE,{"disambiguationData":[OSD([sQuery(id+"F13.wireOp",EDGE,"E109")])]})]});
            var Q7;
            Q7=makeQuery(id+"F14.boolean.opBoolean","INTERSECT",EDGE,{"derivedFrom":[makeQuery(id+"F6.boolean.opBoolean","MERGE",FACE,{"derivedFrom":[makeQuery(id+"F1.opExtrude","SWEPT_FACE",FACE,{"disambiguationData":[OSD([sQuery(id+"F0.wireOp",EDGE,"E13.rect.bottom")])]}),makeQuery(id+"F6.opExtrude","SWEPT_FACE",FACE,{"disambiguationData":[OSD([sQuery(id+"F5.wireOp",EDGE,"E81.bottom")])]})]}),makeQuery(id+"F14.opExtrude","SWEPT_FACE",FACE,{"disambiguationData":[OSD([sQuery(id+"F13.wireOp",EDGE,"E108")])]})]});
            chamfer(context, id + "F15", {"entities" : qUnion([Q0, Q1, Q2, Q3, Q4, Q5, Q6, Q7]), "width" : 1.2 * mm, "tangentPropagation" : true});
        }
    });
